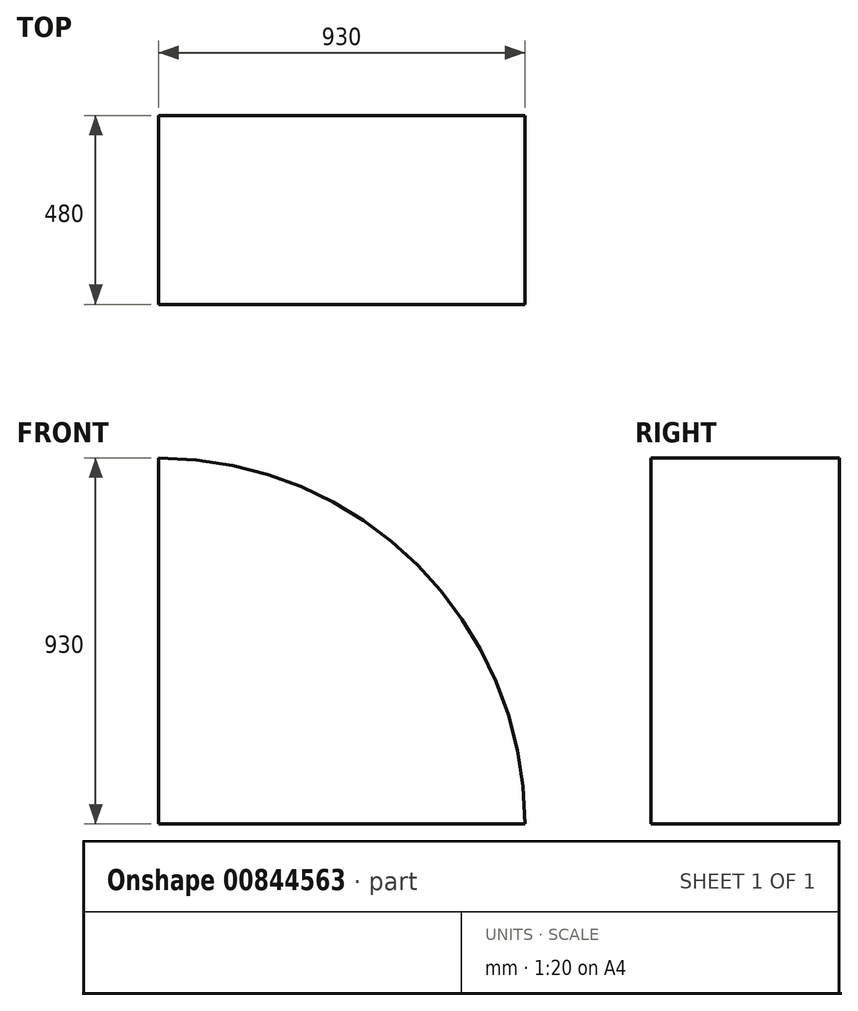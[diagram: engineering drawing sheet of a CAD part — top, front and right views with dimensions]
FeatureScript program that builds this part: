
annotation { "Feature Type Name" : "Feature", "Feature Type Description" : "" }
export const myFeature = defineFeature(function(context is Context, id is Id, definition is map)
    precondition{}
    {
        {
            var Q0;
            Q0=qCreatedBy(makeId("Front.planeOp"),FACE);
            var sketch = newSketch(context, id + "F0", { "sketchPlane" : qUnion([Q0])});
            skArc(sketch, "E0", {"start": v(0, 930) * mm, "mid": v(657.6, 657.6) * mm, "end": v(930, 0) * mm});
            skSolve(sketch);
        }
        {
            var Q0;
            Q0=qCreatedBy(makeId("Right.planeOp"),FACE);
            var sketch = newSketch(context, id + "F1", { "sketchPlane" : qUnion([Q0])});
            skLineSegment(sketch, "E1", {"start": v(0, 930) * mm, "end": v(-480, 930) * mm});
            skSolve(sketch);
        }
        {
            var Q0;
            Q0=qCreatedBy(makeId("Right.planeOp"),FACE);
            var sketch = newSketch(context, id + "F2", { "sketchPlane" : qUnion([Q0])});
            skLineSegment(sketch, "E2.bottom", {"start": v(0, 930) * mm, "end": v(-480, 930) * mm});
            skLineSegment(sketch, "E2.top", {"start": v(0, 0) * mm, "end": v(-480, 0) * mm});
            skLineSegment(sketch, "E2.left", {"start": v(0, 930) * mm, "end": v(0, 0) * mm});
            skLineSegment(sketch, "E2.right", {"start": v(-480, 930) * mm, "end": v(-480, 0) * mm});
            skSolve(sketch);
        }
        {
            var Q0;
            Q0=makeQuery(id+"F2.imprint","IMPRINT",FACE,{"disambiguationData":[TD([[makeQuery(id+"F2.imprint","IMPRINT",EDGE,{"derivedFrom":sQuery(id+"F2.wireOp",EDGE,"E2.bottom")}),1.0]])]});
            var Q1;
            Q1=sQuery(id+"F0.wireOp",EDGE,"E0");
            sweep(context, id + "F3", {"profiles" : qUnion([Q0]), "path" : qUnion([Q1])});
        }
        {
            var Q0;
            Q0=makeQuery(id+"F3.opSweep","CAP_FACE",FACE,{"disambiguationData":[OSD([sQuery(id+"F0.wireOp",VERTEX,"E0.start"),sQuery(id+"F2.wireOp",EDGE,"E2.bottom"),sQuery(id+"F2.wireOp",EDGE,"E2.top"),sQuery(id+"F2.wireOp",EDGE,"E2.left"),sQuery(id+"F2.wireOp",EDGE,"E2.right")])],"isStart":true});
            shell(context, id + "F4", {"entities" : qUnion([Q0]), "thickness" : 0.1 * mm});
        }
    });
